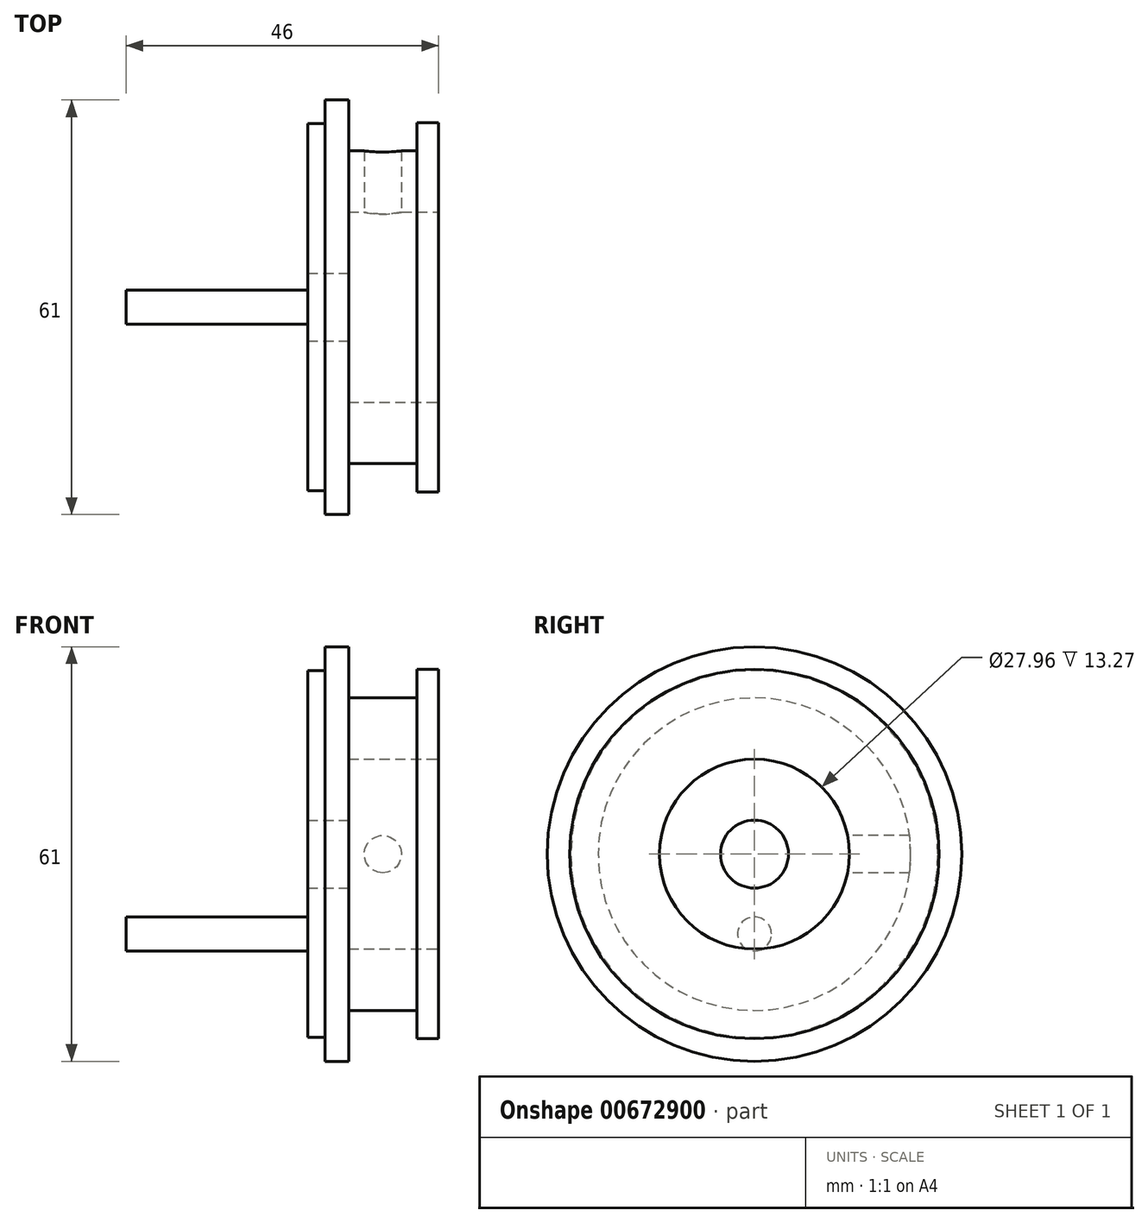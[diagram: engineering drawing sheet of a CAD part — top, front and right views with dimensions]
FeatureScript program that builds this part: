
annotation { "Feature Type Name" : "Feature", "Feature Type Description" : "" }
export const myFeature = defineFeature(function(context is Context, id is Id, definition is map)
    precondition{}
    {
        {
            var Q0;
            Q0=qCreatedBy(makeId("Front.planeOp"),FACE);
            var sketch = newSketch(context, id + "F0", { "sketchPlane" : qUnion([Q0])});
            skLineSegment(sketch, "E0", {"start": v(-23.29, 27) * mm, "end": v(6.01, 27) * mm});
            skLineSegment(sketch, "E1", {"start": v(6.01, 27) * mm, "end": v(6.01, 30.5) * mm});
            skLineSegment(sketch, "E2", {"start": v(6.01, 30.5) * mm, "end": v(9.51, 30.5) * mm});
            skLineSegment(sketch, "E3", {"start": v(9.51, 30.5) * mm, "end": v(9.51, 23) * mm});
            skLineSegment(sketch, "E4", {"start": v(9.51, 23) * mm, "end": v(19.51, 23) * mm});
            skLineSegment(sketch, "E5", {"start": v(19.51, 23) * mm, "end": v(19.51, 27.18) * mm});
            skLineSegment(sketch, "E6", {"start": v(19.51, 27.18) * mm, "end": v(22.71, 27.18) * mm});
            skLineSegment(sketch, "E7", {"start": v(22.71, 27.18) * mm, "end": v(22.71, 13.98) * mm});
            skLineSegment(sketch, "E8", {"start": v(22.71, 13.98) * mm, "end": v(9.44, 13.98) * mm});
            skLineSegment(sketch, "E9", {"start": v(9.44, 13.98) * mm, "end": v(9.44, 5) * mm});
            skLineSegment(sketch, "E10", {"start": v(9.44, 5) * mm, "end": v(-23.29, 5) * mm});
            skPoint(sketch, "E11.end.orphan", {"position": v(-23.29, 13.95) * mm});
            skLineSegment(sketch, "E12", {"start": v(-23.29, 27) * mm, "end": v(-23.29, 5) * mm});
            skSolve(sketch);
        }
        {
            var Q0;
            Q0=qCreatedBy(makeId("Front.planeOp"),FACE);
            var sketch = newSketch(context, id + "F1", { "sketchPlane" : qUnion([Q0])});
            skLineSegment(sketch, "E13", {"start": v(0, 0) * mm, "end": v(90.87, 0) * mm, "construction": true});
            skLineSegment(sketch, "E14", {"start": v(90.87, 0) * mm, "end": v(-118.72, 0) * mm, "construction": true});
            skSolve(sketch);
        }
        {
            var Q0;
            Q0=makeQuery(id+"F0.imprint","IMPRINT",FACE,{"disambiguationData":[TD([[makeQuery(id+"F0.imprint","IMPRINT",EDGE,{"derivedFrom":sQuery(id+"F0.wireOp",EDGE,"E0")}),-1.0]])]});
            var Q1;
            Q1=sQuery(id+"F1.wireOp",EDGE,"E14");
            revolve(context, id + "F2", {"entities" : qUnion([Q0]), "axis" : qUnion([Q1]), "revolveType" : RevolveType.FULL});
        }
        {
            var Q0;
            Q0=qCreatedBy(makeId("Front.planeOp"),FACE);
            var sketch = newSketch(context, id + "F3", { "sketchPlane" : qUnion([Q0])});
            skCircle(sketch, "E15", {"center": v(-3.35, 0) * mm, "radius": 2.5 * mm});
            skSolve(sketch);
        }
        {
            var Q0;
            Q0 = qSketchRegion(id + "F3", true);
            extrude(context, id + "F4", {"entities" : qUnion([Q0]), "operationType" : NewBodyOperationType.REMOVE, "endBound" : BoundingType.SYMMETRIC, "depth" : 113.8 * mm, "offsetDistance" : 25 * mm});
        }
        {
            var Q0;
            Q0=makeQuery(id+"F2.opRevolve","SWEPT_FACE",FACE,{"disambiguationData":[OSD([sQuery(id+"F0.wireOp",EDGE,"E12")])]});
            var sketch = newSketch(context, id + "F5", { "sketchPlane" : qUnion([Q0])});
            skCircle(sketch, "E16", {"center": v(0, 11.75) * mm, "radius": 2.5 * mm});
            skCircle(sketch, "E17.MirrorC", {"center": v(0, -11.75) * mm, "radius": 2.5 * mm});
            skSolve(sketch);
        }
        {
            var Q0;
            Q0=makeQuery(id+"F5.imprint","IMPRINT",FACE,{"disambiguationData":[TD([[makeQuery(id+"F5.imprint","IMPRINT",EDGE,{"derivedFrom":sQuery(id+"F5.wireOp",EDGE,"E17.MirrorC")}),-1.0]])]});
            var Q1;
            Q1=makeQuery(id+"F5.imprint","IMPRINT",FACE,{"disambiguationData":[TD([[makeQuery(id+"F5.imprint","IMPRINT",EDGE,{"derivedFrom":sQuery(id+"F5.wireOp",EDGE,"E16")}),1.0]])]});
            extrude(context, id + "F6", {"entities" : qUnion([Q0, Q1]), "operationType" : NewBodyOperationType.REMOVE, "oppositeDirection" : true, "depth" : 26.75 * mm, "offsetDistance" : 25 * mm});
        }
        {
            var Q0;
            Q0=qCreatedBy(makeId("Front.planeOp"),FACE);
            var sketch = newSketch(context, id + "F7", { "sketchPlane" : qUnion([Q0])});
            skCircle(sketch, "E18", {"center": v(14.51, 0) * mm, "radius": 2.75 * mm});
            skSolve(sketch);
        }
        {
            var Q0;
            Q0 = qSketchRegion(id + "F7", true);
            extrude(context, id + "F8", {"entities" : qUnion([Q0]), "operationType" : NewBodyOperationType.REMOVE, "oppositeDirection" : true, "depth" : 25 * mm, "offsetDistance" : 25 * mm});
        }
    });
